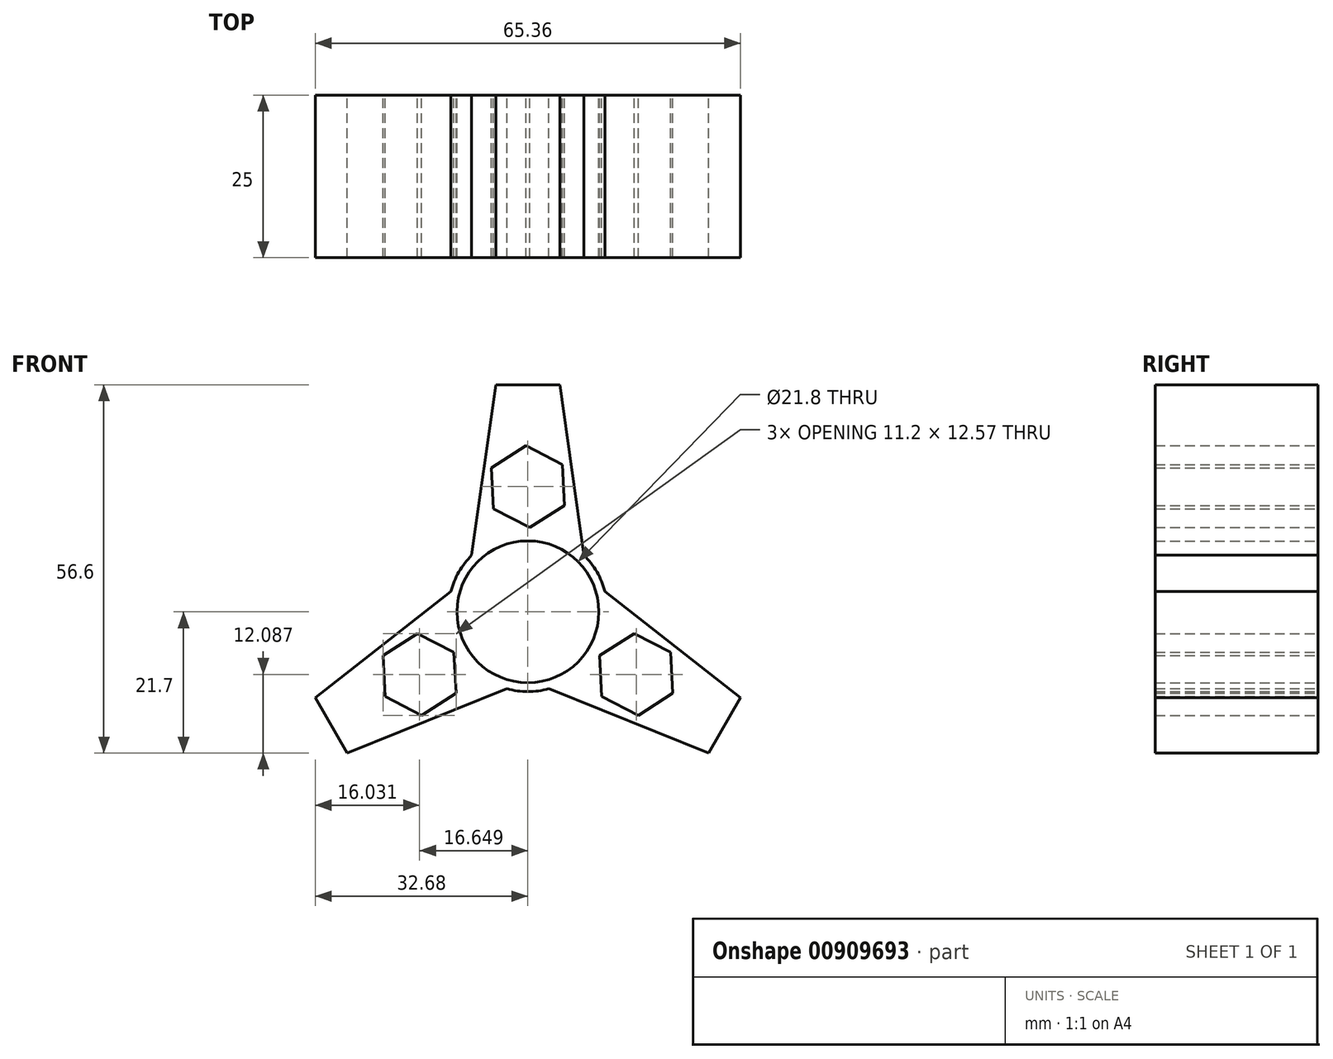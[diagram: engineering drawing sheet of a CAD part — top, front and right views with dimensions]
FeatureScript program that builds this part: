
annotation { "Feature Type Name" : "Feature", "Feature Type Description" : "" }
export const myFeature = defineFeature(function(context is Context, id is Id, definition is map)
    precondition{}
    {
        {
            var Q0;
            Q0=qCreatedBy(makeId("Front.planeOp"),FACE);
            var sketch = newSketch(context, id + "F0", { "sketchPlane" : qUnion([Q0])});
            skLineSegment(sketch, "E0", {"start": v(-8.64, 8.7) * mm, "end": v(-4.9, 34.9) * mm});
            skLineSegment(sketch, "E1", {"start": v(-4.9, 34.9) * mm, "end": v(0, 34.9) * mm});
            skLineSegment(sketch, "E2.MirrorCS", {"start": v(8.64, 8.7) * mm, "end": v(4.9, 34.9) * mm});
            skLineSegment(sketch, "E3", {"start": v(0, 34.9) * mm, "end": v(4.9, 34.9) * mm});
            skCircle(sketch, "E4.cCircle", {"center": v(0, 19.23) * mm, "radius": 5.45 * mm, "construction": true});
            skLineSegment(sketch, "E4.0", {"start": v(0.32, 12.94) * mm, "end": v(-5.28, 15.8) * mm});
            skLineSegment(sketch, "E4.1", {"start": v(-5.28, 15.8) * mm, "end": v(-5.6, 22.1) * mm});
            skLineSegment(sketch, "E4.2", {"start": v(-5.6, 22.1) * mm, "end": v(-0.32, 25.51) * mm});
            skLineSegment(sketch, "E4.3", {"start": v(-0.32, 25.51) * mm, "end": v(5.28, 22.64) * mm});
            skLineSegment(sketch, "E4.4", {"start": v(5.28, 22.64) * mm, "end": v(5.6, 16.36) * mm});
            skLineSegment(sketch, "E4.5", {"start": v(5.6, 16.36) * mm, "end": v(0.32, 12.94) * mm});
            skPoint(sketch, "E4.0.midPoint", {"position": v(-2.48, 14.37) * mm});
            skLineSegment(sketch, "E5.1.0", {"start": v(-3.22, -11.83) * mm, "end": v(-27.77, -21.7) * mm});
            skLineSegment(sketch, "E5.1.1", {"start": v(-27.77, -21.7) * mm, "end": v(-30.23, -17.45) * mm});
            skLineSegment(sketch, "E5.2.0", {"start": v(11.85, 3.13) * mm, "end": v(32.68, -13.2) * mm});
            skLineSegment(sketch, "E5.2.1", {"start": v(32.68, -13.2) * mm, "end": v(30.23, -17.45) * mm});
            skPoint(sketch, "E5.center", {"position": v(0, 0) * mm});
            skLineSegment(sketch, "E6.1.0", {"start": v(-30.23, -17.45) * mm, "end": v(-32.68, -13.2) * mm});
            skLineSegment(sketch, "E6.2.0", {"start": v(30.23, -17.45) * mm, "end": v(27.77, -21.7) * mm});
            skLineSegment(sketch, "E7.1.0", {"start": v(-11.85, 3.13) * mm, "end": v(-32.68, -13.2) * mm});
            skCircle(sketch, "E7.1.1", {"center": v(-16.65, -9.61) * mm, "radius": 5.45 * mm, "construction": true});
            skLineSegment(sketch, "E7.1.2", {"start": v(-21.93, -13.03) * mm, "end": v(-22.25, -6.74) * mm});
            skLineSegment(sketch, "E7.1.3", {"start": v(-16.33, -15.9) * mm, "end": v(-21.93, -13.03) * mm});
            skLineSegment(sketch, "E7.1.4", {"start": v(-11.05, -12.48) * mm, "end": v(-16.33, -15.9) * mm});
            skLineSegment(sketch, "E7.1.5", {"start": v(-11.36, -6.2) * mm, "end": v(-11.05, -12.48) * mm});
            skLineSegment(sketch, "E7.1.6", {"start": v(-16.97, -3.33) * mm, "end": v(-11.36, -6.2) * mm});
            skLineSegment(sketch, "E7.1.7", {"start": v(-22.25, -6.74) * mm, "end": v(-16.97, -3.33) * mm});
            skLineSegment(sketch, "E7.2.0", {"start": v(3.22, -11.83) * mm, "end": v(27.77, -21.7) * mm});
            skCircle(sketch, "E7.2.1", {"center": v(16.65, -9.61) * mm, "radius": 5.45 * mm, "construction": true});
            skLineSegment(sketch, "E7.2.2", {"start": v(22.25, -12.48) * mm, "end": v(16.97, -15.9) * mm});
            skLineSegment(sketch, "E7.2.3", {"start": v(21.93, -6.2) * mm, "end": v(22.25, -12.48) * mm});
            skLineSegment(sketch, "E7.2.4", {"start": v(16.33, -3.33) * mm, "end": v(21.93, -6.2) * mm});
            skLineSegment(sketch, "E7.2.5", {"start": v(11.05, -6.74) * mm, "end": v(16.33, -3.33) * mm});
            skLineSegment(sketch, "E7.2.6", {"start": v(11.36, -13.03) * mm, "end": v(11.05, -6.74) * mm});
            skLineSegment(sketch, "E7.2.7", {"start": v(16.97, -15.9) * mm, "end": v(11.36, -13.03) * mm});
            skCircle(sketch, "E8", {"center": v(0, 0) * mm, "radius": 10.9 * mm});
            skArc(sketch, "E9", {"start": v(-3.22, -11.83) * mm, "mid": v(0, -12.26) * mm, "end": v(3.22, -11.83) * mm});
            skPoint(sketch, "E10.start.orphan", {"position": v(-8.97, 6.38) * mm});
            skArc(sketch, "E11.trimOffspring", {"start": v(-8.64, 8.7) * mm, "mid": v(-10.61, 6.13) * mm, "end": v(-11.85, 3.13) * mm});
            skPoint(sketch, "E12.trimOffspring.end.orphan", {"position": v(8.97, 6.38) * mm});
            skPoint(sketch, "E13.orphan", {"position": v(10, 4.57) * mm});
            skArc(sketch, "E14.trimOffspring", {"start": v(11.85, 3.13) * mm, "mid": v(10.61, 6.13) * mm, "end": v(8.64, 8.7) * mm});
            skPoint(sketch, "E15.orphan", {"position": v(1.04, -10.95) * mm});
            skSolve(sketch);
        }
        {
            var Q0;
            Q0=makeQuery(id+"F0.imprint","IMPRINT",FACE,{"disambiguationData":[TD([[makeQuery(id+"F0.imprint","IMPRINT",EDGE,{"derivedFrom":sQuery(id+"F0.wireOp",EDGE,"E0")}),-1.0]])]});
            extrude(context, id + "F1", {"entities" : qUnion([Q0]), "depth" : 25 * mm, "offsetDistance" : 25 * mm});
        }
    });
